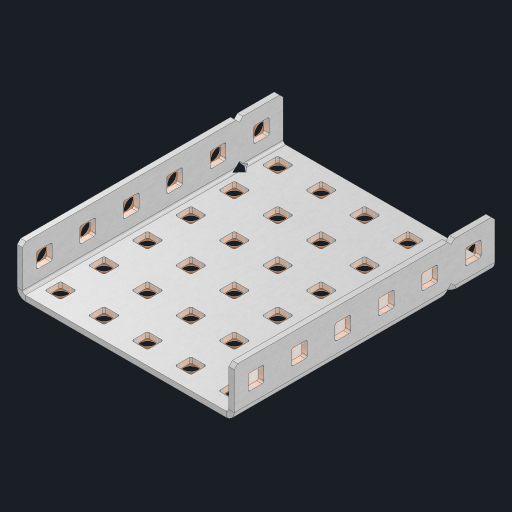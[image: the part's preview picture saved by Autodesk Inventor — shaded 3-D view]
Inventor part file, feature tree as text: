
AUTODESK INVENTOR PART (.ipt)
format: ipt  version: 2023 (Build 270158000, 158)  size: 774,656 bytes
history: native  units: in
note: dims shown in document units (in); Inventor stores cm internally (conversion verified against a paired STEP export)
features: other x47, extrude x41, sheet_metal_op x10, sketch x8, mirror x1, pattern_linear x1, chamfer x1
ambient origin geometry x8: Origin, YZ Plane, XZ Plane, XY Plane, X Axis, Y Axis, Z Axis, Center Point
bodies: Solid1 (feature_tree), Body (feature_tree)
feature tree (109):
  other  "Flange Pattern Plane"
  sheet_metal_op  "Flange Pattern"
  sheet_metal_op  "Body Pattern"
  other  "Arc Length"
  mirror  "Notch Mirror"
  pattern_linear  "Notch Pattern"  Spacing1=0.25in  [1 undecoded]
  chamfer  "End Chamfer"
  extrude  "Half Cut"  Depth=0.0625in
  sketch  "Sketch1"  dims[d0=2.5in]
  other  "Plate1"
  sketch  "Sketch2"  dims[d1=3.0in]
  other  "Plate2"
  sheet_metal_op  "Bend1"
  sheet_metal_op  "Corner1"
  sketch  "Sketch3"  dims[d2=0.0625in]
  other  "Flange Pattern Sketch"
  sketch  "Sketch7"  dims[d3=0.0625in]
  other  "Srf1"
  other  "Srf2"
  sketch  "Sketch8"  dims[d4=0.0312in]
  sketch  "Sketch9"  dims[d5=0.125in]
  other  "Srf91"
  sheet_metal_op  "Body Pattern Sketch"
  other  "Srf92"
  sketch  "Sketch13"  dims[d6=0.0625in]
  sketch  "Sketch14"  dims[d7=0.5in d8=90.0deg d9=0.0312in d10=0.25in d11=0.0625in d12=0.0625in d16=0.182in d17=0.02in d18=0.0625in d19=0.0in d20=0.25in d21=0.25in d46=0.172in d47=1.0in d48=0.0in d49=0.182in d50=0.02in d51=0.25in d52=0.25in d53=0.0625in d54=0.0in d55=0.172in d56=1.0in d57=0.0in d60=2.3622in d62=0.5in d63=1.9685in d65=0.5in d85=0.1473in d86=0.1782in d88=0.04in d89=0.0625in d90=0.0in d91=0.04in d92=0.0491in d95=2.5in d96=0.04in d97=0.25in d98=45.0deg d101=0.0in d102=2.497in d131=2.5in d132=2.3622in d134=0.5in d139=0.5in]
  other  "Srf856"
  other  "Srf1310"
  other  "Srf1311"
  other  "Srf1312"
  other  "Srf1376"
  other  "Srf1377"
  other  "Srf1728"
  other  "Srf1755"
  other  "Srf1878"
  other  "Srf1879"
  other  "Srf1880"
  other  "Srf1881"
  other  "Srf1882"
  other  "Srf1883"
  other  "Srf1942"
  other  "Srf1943"
  other  "Srf1944"
  other  "Srf1945"
  other  "Srf1946"
  other  "Srf1947"
  other  "Srf1948"
  other  "Srf1949"
  other  "Srf1950"
  other  "Srf1951"
  other  "Srf1952"
  other  "Srf1953"
  other  "Srf1954"
  other  "Srf1955"
  other  "Srf1956"
  other  "Srf1957"
  other  "Srf1958"
  other  "Srf1959"
  other  "Srf1960"
  other  "Srf1961"
  other  "Srf1962"
  other  "Srf1963"
  other  "Srf1964"
  other  "Srf1965"
  sheet_metal_op  "Flange Stamp"
  sheet_metal_op  "Flange Circle"
  sheet_metal_op  "Body Stamp"
  sheet_metal_op  "Body Circle"
  sheet_metal_op  "Notch"
  extrude  "ExtrusionSrf2"  Depth=0.0625in
  extrude  "ExtrusionSrf92"  Depth=2.5in
  extrude  "ExtrusionSrf856"  Depth=0.02in
  extrude  "ExtrusionSrf1310"  Depth=0.0625in
  extrude  "ExtrusionSrf1311"  TaperAngle=0.0deg  [1 undecoded]
  extrude  "ExtrusionSrf1312"  Depth=0.25in
  extrude  "ExtrusionSrf1376"  Depth=0.25in
  extrude  "ExtrusionSrf1377"  Depth=2.5in
  extrude  "ExtrusionSrf1728"  Depth=2.5in TaperAngle=0.0deg
  extrude  "ExtrusionSrf1755"  Depth=2.5in
  extrude  "ExtrusionSrf1878"  Depth=0.02in
  extrude  "ExtrusionSrf1879"  Depth=0.25in
  extrude  "ExtrusionSrf1880"  Depth=0.25in
  extrude  "ExtrusionSrf1881"  Depth=0.0625in
  extrude  "ExtrusionSrf1882"  TaperAngle=0.0deg  [1 undecoded]
  extrude  "ExtrusionSrf1883"  Depth=2.5in
  extrude  "ExtrusionSrf1942"  Depth=2.5in TaperAngle=0.0deg
  extrude  "ExtrusionSrf1943"  Depth=2.5in
  extrude  "ExtrusionSrf1944"  Depth=2.5in
  extrude  "ExtrusionSrf1945"  Depth=2.5in
  extrude  "ExtrusionSrf1946"  Depth=2.5in
  extrude  "ExtrusionSrf1947"  Depth=2.5in
  extrude  "ExtrusionSrf1948"  Depth=0.0625in
  extrude  "ExtrusionSrf1949"  TaperAngle=0.0deg  [1 undecoded]
  extrude  "ExtrusionSrf1950"  Depth=2.5in
  extrude  "ExtrusionSrf1951"  Depth=2.5in
  extrude  "ExtrusionSrf1952"  Depth=2.5in
  extrude  "ExtrusionSrf1953"  Depth=0.25in TaperAngle=45.0deg
  extrude  "ExtrusionSrf1954"  TaperAngle=0.0deg  [1 undecoded]
  extrude  "ExtrusionSrf1955"  Depth=2.5in
  extrude  "ExtrusionSrf1956"  Depth=2.5in
  extrude  "ExtrusionSrf1957"  Depth=2.5in
  extrude  "ExtrusionSrf1958"  Depth=2.5in
  extrude  "ExtrusionSrf1959"  Depth=2.5in
  extrude  "ExtrusionSrf1960"  [1 undecoded]
  extrude  "ExtrusionSrf1961"  [1 undecoded]
  extrude  "ExtrusionSrf1962"  [1 undecoded]
  extrude  "ExtrusionSrf1963"  [1 undecoded]
  extrude  "ExtrusionSrf1964"  [1 undecoded]
  extrude  "ExtrusionSrf1965"  [1 undecoded]
note: 11 required parameter values undecoded (feature->parameter linkage not recoverable at this tier; creation-order binding heuristic only, values carry confidence <= 0.55)
